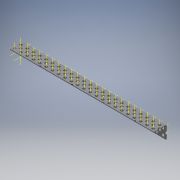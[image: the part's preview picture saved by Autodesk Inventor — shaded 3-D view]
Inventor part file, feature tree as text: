
AUTODESK INVENTOR PART (.ipt)
format: ipt  version: 2017 SP1 (Build 210196100, 196)  size: 2,191,360 bytes
history: native  units: in
note: dims shown in document units (in); Inventor stores cm internally (conversion verified against a paired STEP export)
features: other x143, pattern_linear x4, sheet_metal_op x1, extrude x1, imported_body x1, sketch x1
ambient origin geometry x8: Origin, YZ Plane, XZ Plane, XY Plane, X Axis, Y Axis, Z Axis, Center Point
bodies: Body1 (feature_tree)
feature tree (151):
  sheet_metal_op  "Fold1"
  other  "L-Channel"
  extrude  "length cut"  Depth=0.5in
  other  "top out axis"
  other  "top inner axis"
  other  "back out axis"
  other  "back inner axis"
  pattern_linear  "top outer axes"  Count1=2 Spacing1=0.5in
  pattern_linear  "top inner axes"  Spacing1=0.5in  [1 undecoded]
  pattern_linear  "back outer axes"  Count1=2 Spacing1=0.5in
  pattern_linear  "back inner axes"  Spacing1=0.5in  [1 undecoded]
  other  "right plane"
  imported_body  "Base1"
  sketch  "Sketch1"  dims[d1=0.0in d4=0.5in d5=0.7874in d7=0.5in d10=0.5in d13=0.5in d14=0.7874in d16=0.5in d19=0.5in d20=-11.5in d21=0.0in d22=0.0in d23=0.0in d24=0.0in d25=0.0in d26=0.0in]
  other  "Work Point1"
  other  "Work Point2"
  other  "Work Point3"
  other  "Work Point4"
  other  "Work Axis5"
  other  "Work Axis6"
  other  "Work Axis7"
  other  "Work Axis11"
  other  "Work Axis12"
  other  "Work Axis13"
  other  "Work Axis14"
  other  "Work Axis18"
  other  "Work Axis19"
  other  "Work Axis23"
  other  "Work Axis24"
  other  "Work Axis25"
  other  "Work Axis29"
  other  "Work Axis30"
  other  "Work Axis31"
  other  "Work Axis32"
  other  "Work Axis36"
  other  "Work Axis37"
  other  "left plane"
  other  "Work Axis173"
  other  "Work Axis174"
  other  "Work Axis175"
  other  "Work Axis176"
  other  "Work Axis177"
  other  "Work Axis178"
  other  "Work Axis179"
  other  "Work Axis180"
  other  "Work Axis181"
  other  "Work Axis182"
  other  "Work Axis183"
  other  "Work Axis184"
  other  "Work Axis185"
  other  "Work Axis186"
  other  "Work Axis187"
  other  "Work Axis188"
  other  "Work Axis189"
  other  "Work Axis190"
  other  "Work Axis191"
  other  "Work Axis192"
  other  "Work Axis193"
  other  "Work Axis194"
  other  "Work Axis195"
  other  "Work Axis196"
  other  "Work Axis197"
  other  "Work Axis198"
  other  "Work Axis199"
  other  "Work Axis200"
  other  "Work Axis201"
  other  "Work Axis202"
  other  "Work Axis203"
  other  "Work Axis204"
  other  "Work Axis205"
  other  "Work Axis206"
  other  "Work Axis207"
  other  "Work Axis208"
  other  "Work Axis209"
  other  "Work Axis210"
  other  "Work Axis211"
  other  "Work Axis212"
  other  "Work Axis213"
  other  "Work Axis214"
  other  "Work Axis215"
  other  "Work Axis216"
  other  "Work Axis217"
  other  "Work Axis218"
  other  "Work Axis219"
  other  "Work Axis220"
  other  "Work Axis221"
  other  "Work Axis222"
  other  "Work Axis223"
  other  "Work Axis224"
  other  "Work Axis225"
  other  "Work Axis226"
  other  "Work Axis227"
  other  "Work Axis228"
  other  "Work Axis229"
  other  "Work Axis230"
  other  "Work Axis231"
  other  "Work Axis232"
  other  "Work Axis233"
  other  "Work Axis234"
  other  "Work Axis235"
  other  "Work Axis236"
  other  "Work Axis237"
  other  "Work Axis238"
  other  "Work Axis239"
  other  "Work Axis240"
  other  "Work Axis241"
  other  "Work Axis242"
  other  "Work Axis243"
  other  "Work Axis244"
  other  "Work Axis245"
  other  "Work Axis246"
  other  "Work Axis247"
  other  "Work Axis248"
  other  "Work Axis249"
  other  "Work Axis250"
  other  "Work Axis251"
  other  "Work Axis252"
  other  "Work Axis253"
  other  "Work Axis254"
  other  "Work Axis255"
  other  "Work Axis256"
  other  "Work Axis257"
  other  "Work Axis258"
  other  "Work Axis259"
  other  "Work Axis260"
  other  "Work Axis261"
  other  "Work Axis262"
  other  "Work Axis263"
  other  "Work Axis264"
  other  "Work Axis265"
  other  "Work Axis266"
  other  "Work Axis267"
  other  "Work Axis268"
  other  "Work Axis269"
  other  "Work Axis270"
  other  "Work Axis271"
  other  "Work Axis272"
  other  "Work Axis273"
  other  "Work Axis274"
  other  "Work Axis275"
  other  "Work Axis276"
  other  "Work Axis277"
  other  "Work Axis278"
  other  "Work Axis279"
  other  "Work Axis280"
  other  "Work Axis281"
  other  "Work Axis282"
  other  "Work Axis283"
  other  "Work Axis284"
  other  "Work Axis285"
  other  "Work Axis286"
note: 2 required parameter values undecoded (feature->parameter linkage not recoverable at this tier; creation-order binding heuristic only, values carry confidence <= 0.55)
